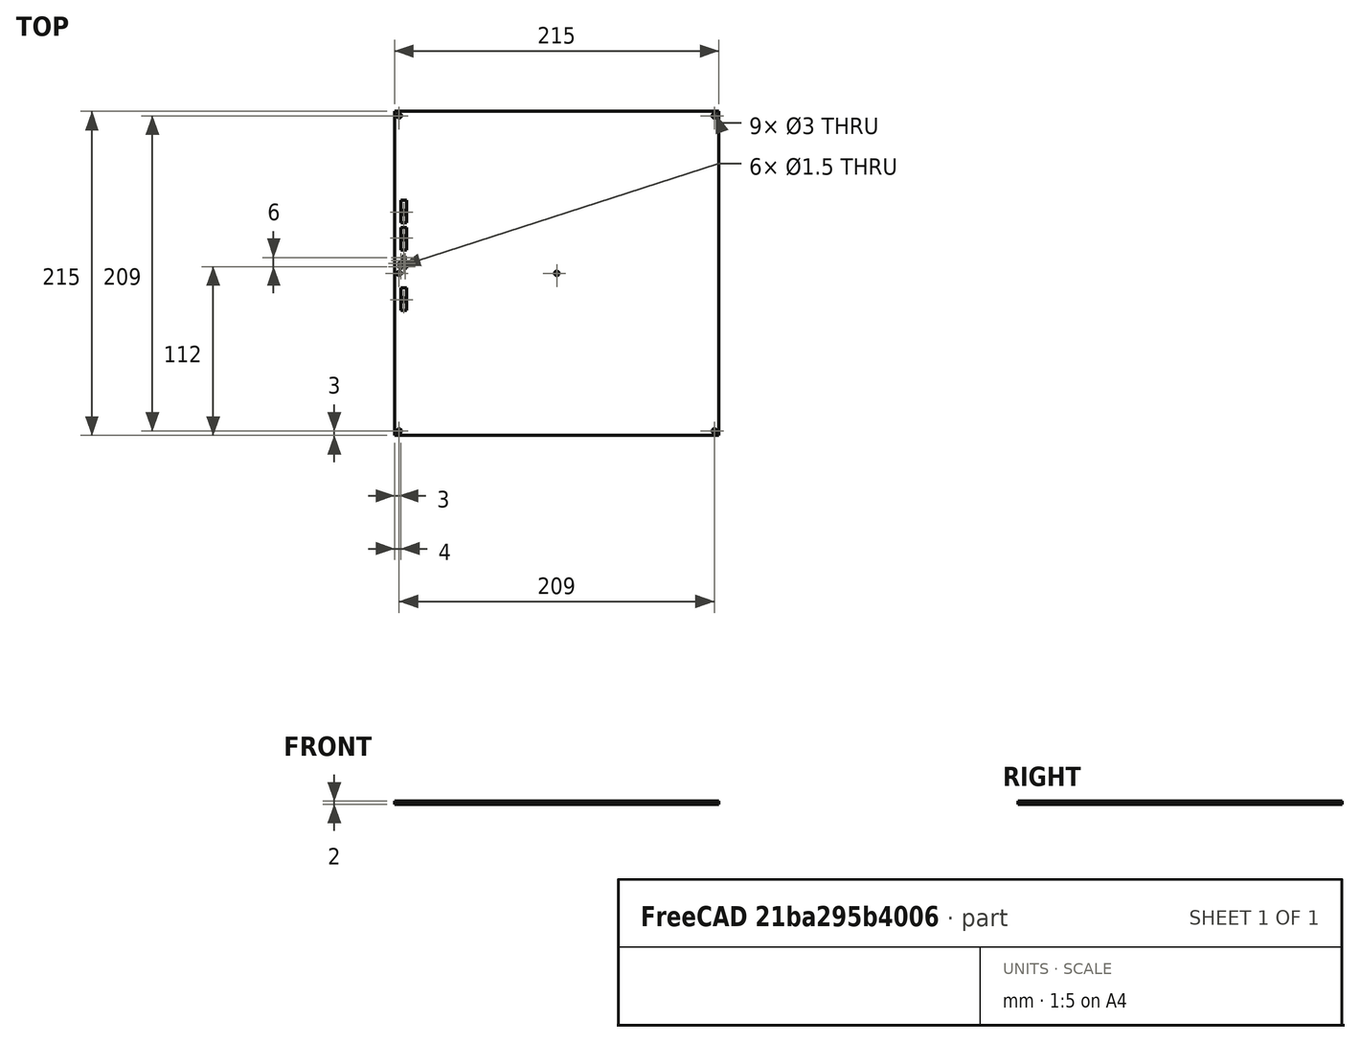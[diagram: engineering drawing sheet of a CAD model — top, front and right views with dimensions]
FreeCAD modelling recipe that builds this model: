
FCSTD DOCUMENT  (FreeCAD 0.16R6707 (Git))
Label: heat_bed
License: CC-BY 3.0
LicenseURL: http://creativecommons.org/licenses/by/3.0/
objects: Part::Cut×21, Part::Cylinder×15, Part::Box×7, Raytracing::RayFeature×1, Raytracing::RayProject×1
note: 43 computed .brp shape members not serialized (recipe doc carries the construction recipe); baked Part::Feature solids carry a one-line shape summary decoded from their .brp

FEATURE [Part::Box] Box  label="Cube"
  Height = 2
  Length = 215
  Width = 215
FEATURE [Part::Cylinder] Cylinder
  Angle = 360
  Height = 10
  Placement = pos=(212,3,0) rot=(0,0,1;0rad)
  Radius = 1.5
FEATURE [Part::Cylinder] Cylinder001
  Angle = 360
  Height = 10
  Placement = pos=(3,3,0) rot=(0,0,1;0rad)
  Radius = 1.5
FEATURE [Part::Cylinder] Cylinder002
  Angle = 360
  Height = 10
  Placement = pos=(212,212,0) rot=(0,0,1;0rad)
  Radius = 1.5
FEATURE [Part::Cylinder] Cylinder003
  Angle = 360
  Height = 10
  Placement = pos=(3,212,0) rot=(0,0,1;0rad)
  Radius = 1.5
FEATURE [Part::Cylinder] Cylinder004
  Angle = 360
  Height = 10
  Placement = pos=(107.5,107.5,0) rot=(0,0,1;0rad)
  Radius = 1.5
FEATURE [Part::Cylinder] Cylinder005
  Angle = 360
  Height = 10
  Placement = pos=(6,90,0) rot=(0,0,1;0rad)
  Radius = 1.5
FEATURE [Part::Cylinder] Cylinder006
  Angle = 360
  Height = 10
  Placement = pos=(3,107.5,0) rot=(0,0,1;0rad)
  Radius = 1.5
FEATURE [Part::Cylinder] Cylinder007
  Angle = 360
  Height = 10
  Placement = pos=(6,131,0) rot=(0,0,1;0rad)
  Radius = 1.5
FEATURE [Part::Cylinder] Cylinder008
  Angle = 360
  Height = 10
  Placement = pos=(6,148,0) rot=(0,0,1;0rad)
  Radius = 1.5
FEATURE [Part::Cylinder] Cylinder009
  Angle = 360
  Height = 10
  Placement = pos=(4,112,0) rot=(0,0,1;0rad)
  Radius = 0.75
FEATURE [Part::Cut] Cut
  Base = -> Box
  Tool = -> Cylinder001
FEATURE [Part::Cut] Cut001
  Base = -> Cut
  Tool = -> Cylinder
FEATURE [Part::Cut] Cut002
  Base = -> Cut001
  Tool = -> Cylinder002
FEATURE [Part::Cut] Cut003
  Base = -> Cut002
  Tool = -> Cylinder004
FEATURE [Part::Cut] Cut004
  Base = -> Cut003
  Tool = -> Cylinder003
FEATURE [Part::Cut] Cut005
  Base = -> Cut004
  Tool = -> Cylinder005
FEATURE [Part::Cut] Cut006
  Base = -> Cut005
  Tool = -> Cylinder008
FEATURE [Part::Cut] Cut007
  Base = -> Cut006
  Tool = -> Cylinder007
FEATURE [Part::Cut] Cut008
  Base = -> Cut007
  Tool = -> Cylinder006
FEATURE [Part::Cylinder] Cylinder010
  Angle = 360
  Height = 10
  Placement = pos=(4,114,0) rot=(0,0,1;0rad)
  Radius = 0.75
FEATURE [Part::Cylinder] Cylinder011
  Angle = 360
  Height = 10
  Placement = pos=(6,116,0) rot=(0,0,1;0rad)
  Radius = 0.75
FEATURE [Part::Cylinder] Cylinder012
  Angle = 360
  Height = 10
  Placement = pos=(6,118,0) rot=(0,0,1;0rad)
  Radius = 0.75
FEATURE [Part::Cylinder] Cylinder013
  Angle = 360
  Height = 10
  Placement = pos=(7,112,0) rot=(0,0,1;0rad)
  Radius = 0.75
FEATURE [Part::Cylinder] Cylinder014
  Angle = 360
  Height = 10
  Placement = pos=(7,114,0) rot=(0,0,1;0rad)
  Radius = 0.75
FEATURE [Part::Cut] Cut009
  Base = -> Cut008
  Tool = -> Cylinder009
FEATURE [Part::Cut] Cut010
  Base = -> Cut009
  Tool = -> Cylinder013
FEATURE [Part::Cut] Cut011
  Base = -> Cut010
  Tool = -> Cylinder014
FEATURE [Part::Cut] Cut012
  Base = -> Cut011
  Tool = -> Cylinder010
FEATURE [Part::Cut] Cut013
  Base = -> Cut012
  Tool = -> Cylinder011
FEATURE [Part::Cut] Cut014
  Base = -> Cut013
  Tool = -> Cylinder012
FEATURE [Part::Box] Box001  label="Cube001"
  Height = 0.5
  Length = 4
  Placement = pos=(4,83,1.75) rot=(0,0,1;0rad)
  Width = 15
FEATURE [Part::Box] Box002  label="Cube002"
  Height = 0.5
  Length = 4
  Placement = pos=(4,123,1.75) rot=(0,0,1;0rad)
  Width = 15
FEATURE [Part::Box] Box003  label="Cube003"
  Height = 0.5
  Length = 4
  Placement = pos=(4,141,1.75) rot=(0,0,1;0rad)
  Width = 15
FEATURE [Part::Box] Box004  label="Cube004"
  Height = 0.5
  Length = 2
  Placement = pos=(3,111,1.75) rot=(0,0,1;0rad)
  Width = 4
FEATURE [Part::Cut] Cut015
  Base = -> Cut014
  Tool = -> Box001
FEATURE [Part::Cut] Cut016
  Base = -> Cut015
  Tool = -> Box002
FEATURE [Part::Cut] Cut017
  Base = -> Cut016
  Tool = -> Box003
FEATURE [Part::Box] Box005  label="Cube005"
  Height = 0.5
  Length = 2
  Placement = pos=(6,111,1.75) rot=(0,0,1;0rad)
  Width = 4
FEATURE [Part::Box] Box006  label="Cube006"
  Height = 0.5
  Length = 2
  Placement = pos=(5,115,1.75) rot=(0,0,1;0rad)
  Width = 4
FEATURE [Part::Cut] Cut018
  Base = -> Cut017
  Tool = -> Box004
FEATURE [Part::Cut] Cut019
  Base = -> Cut018
  Tool = -> Box006
FEATURE [Part::Cut] Cut020
  Base = -> Cut019
  Tool = -> Box005
FEATURE [Raytracing::RayFeature] Cut020_View
  Result = <blob: 112923 chars omitted>
  Source = -> Cut020
  Transparency = 0
FEATURE [Raytracing::RayProject] PovProject
  Camera = // declares positon and view direction\n\n// Generated by FreeCAD (http://www.freecadweb.org/)\n#declare cam_location =  <-121.592,-332.82,-84.9878>;\n#declare cam_look_at  = <107.498,1.00323,107.501>;\n#declare cam_sky      = <0.567326,-0.667456,0.482332>;\n#declare cam_angle    = 45; \ncamera {\n  location  cam_location\n  look_at   cam_look_at\n  sky       cam_sky\n  angle     cam_angle \n  right x*800/600\n}
  Group = -> [Cut020_View]
